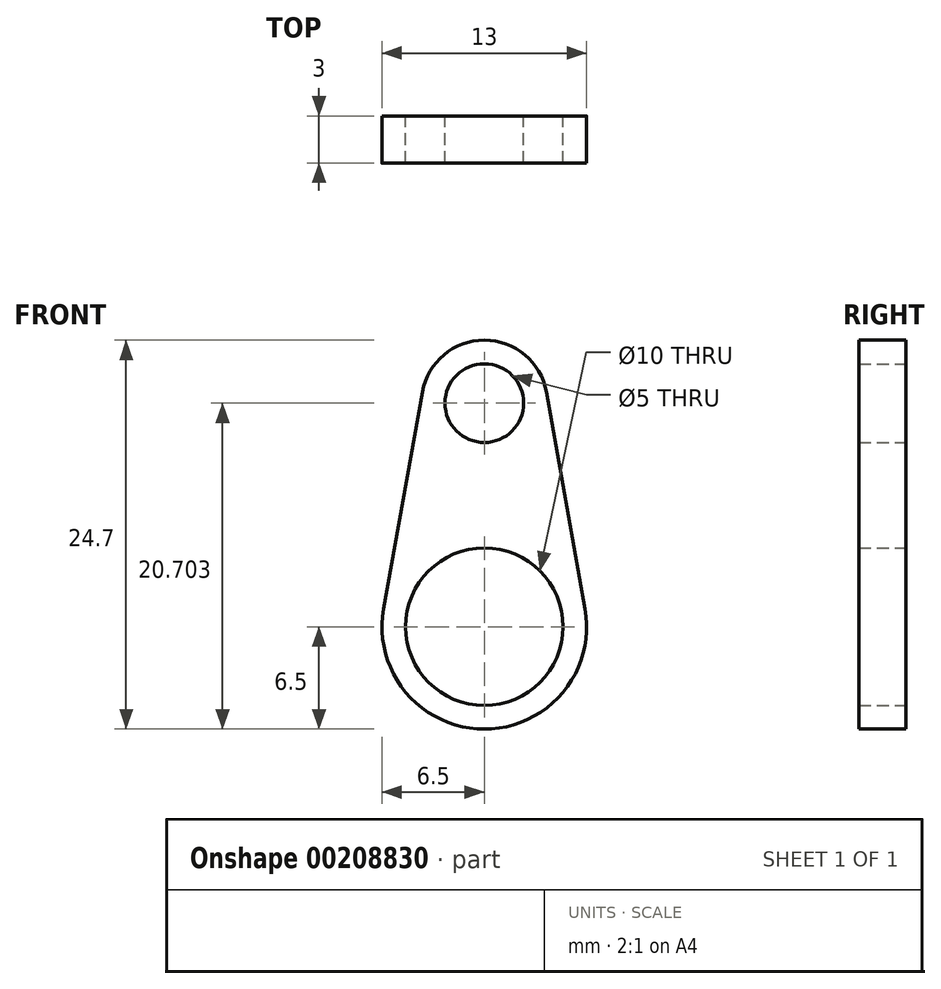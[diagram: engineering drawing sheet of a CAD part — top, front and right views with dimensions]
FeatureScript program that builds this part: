
annotation { "Feature Type Name" : "Feature", "Feature Type Description" : "" }
export const myFeature = defineFeature(function(context is Context, id is Id, definition is map)
    precondition{}
    {
        {
            var Q0;
            Q0=qCreatedBy(makeId("Front.planeOp"),FACE);
            var sketch = newSketch(context, id + "F0", { "sketchPlane" : qUnion([Q0])});
            skCircle(sketch, "E0", {"center": v(0, 0) * mm, "radius": 5 * mm});
            skCircle(sketch, "E1", {"center": v(0, 14.2) * mm, "radius": 2.5 * mm});
            skLineSegment(sketch, "E2", {"start": v(5.08, 0) * mm, "end": v(4.92, 0.88) * mm});
            skArc(sketch, "E3", {"start": v(-4.92, 0.88) * mm, "mid": v(0, -5) * mm, "end": v(4.92, 0.88) * mm});
            skArc(sketch, "E4", {"start": v(2.46, 14.64) * mm, "mid": v(0, 16.7) * mm, "end": v(-2.46, 14.64) * mm});
            skLineSegment(sketch, "E5.0", {"start": v(3.94, 14.9) * mm, "end": v(6.4, 1.14) * mm});
            skArc(sketch, "E5.1", {"start": v(3.94, 14.9) * mm, "mid": v(0, 18.2) * mm, "end": v(-3.94, 14.9) * mm});
            skLineSegment(sketch, "E5.2", {"start": v(-3.94, 14.9) * mm, "end": v(-6.4, 1.14) * mm});
            skArc(sketch, "E5.3", {"start": v(-6.4, 1.14) * mm, "mid": v(0, -6.5) * mm, "end": v(6.4, 1.14) * mm});
            skPoint(sketch, "E6.end.orphan", {"position": v(4.92, 0.88) * mm});
            skPoint(sketch, "E6.start.orphan", {"position": v(2.46, 14.64) * mm});
            skPoint(sketch, "E7.MirrorCS.end.orphan", {"position": v(-4.92, 0.88) * mm});
            skPoint(sketch, "E7.MirrorCS.start.orphan", {"position": v(-2.46, 14.64) * mm});
            skSolve(sketch);
        }
        {
            var Q0;
            Q0=makeQuery(id+"F0.imprint","IMPRINT",FACE,{"disambiguationData":[TD([[makeQuery(id+"F0.imprint","IMPRINT",EDGE,{"derivedFrom":sQuery(id+"F0.wireOp",EDGE,"E5.0")}),-1.0]])]});
            extrude(context, id + "F1", {"entities" : qUnion([Q0]), "depth" : 3 * mm});
        }
    });
